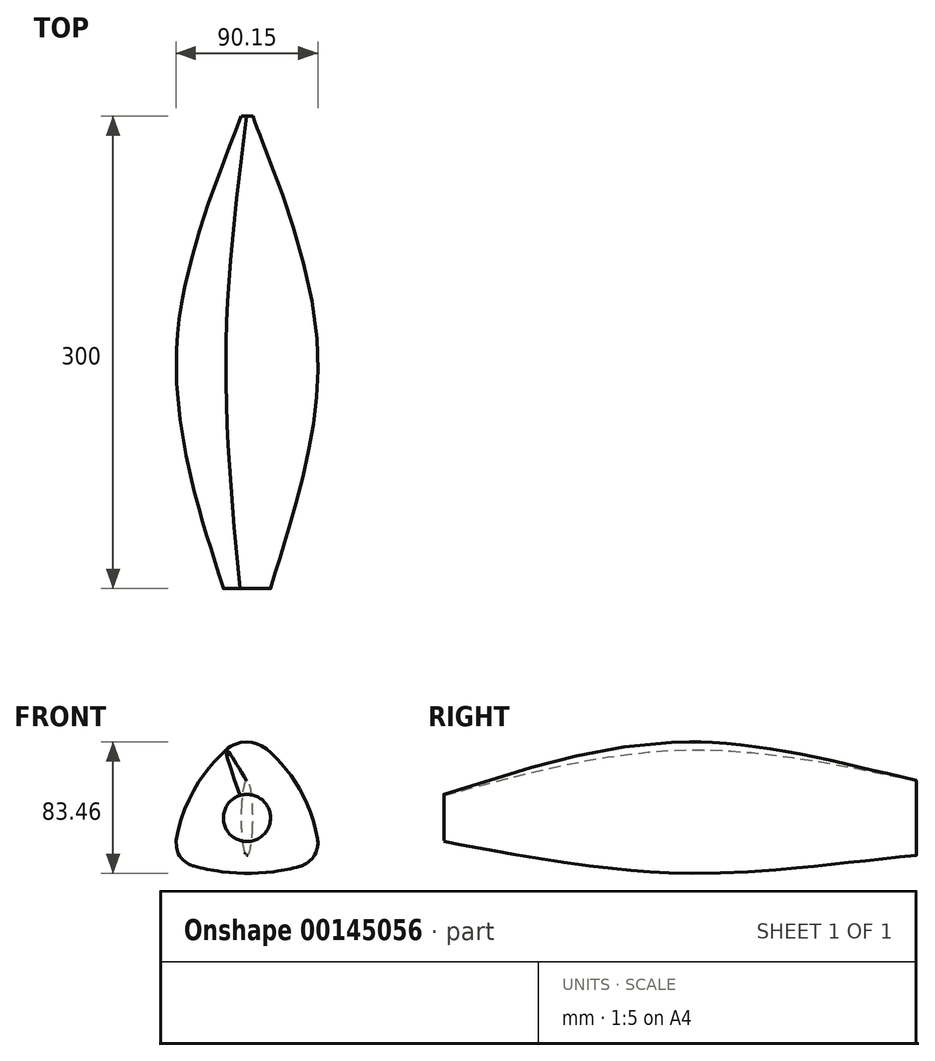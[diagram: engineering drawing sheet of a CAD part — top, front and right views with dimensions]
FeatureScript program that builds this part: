
annotation { "Feature Type Name" : "Feature", "Feature Type Description" : "" }
export const myFeature = defineFeature(function(context is Context, id is Id, definition is map)
    precondition{}
    {
        {
            var Q0;
            Q0=qCreatedBy(makeId("Front.planeOp"),FACE);
            var sketch = newSketch(context, id + "F0", { "sketchPlane" : qUnion([Q0])});
            skCircle(sketch, "E0", {"center": v(0, 0) * mm, "radius": 15 * mm});
            skSolve(sketch);
        }
        {
            var Q0;
            Q0=qCreatedBy(makeId("Front.planeOp"),FACE);
            cPlane(context, id + "F1", {"entities" : qUnion([Q0]), "cplaneType" : CPlaneType.OFFSET, "offset" : 150 * mm, "oppositeDirection" : true, "width" : 150 * mm, "height" : 150 * mm});
        }
        {
            var Q0;
            Q0=qCreatedBy(id+"F1.planeOp",FACE);
            var sketch = newSketch(context, id + "F2", { "sketchPlane" : qUnion([Q0])});
            skArc(sketch, "E1", {"start": v(-13.38, 43.09) * mm, "mid": v(-33.79, 17.42) * mm, "end": v(-44.7, -13.51) * mm});
            skArc(sketch, "E2", {"start": v(44.7, -13.51) * mm, "mid": v(33.79, 17.42) * mm, "end": v(13.38, 43.09) * mm});
            skArc(sketch, "E3", {"start": v(-33.82, -30.57) * mm, "mid": v(0, -35.05) * mm, "end": v(33.82, -30.57) * mm});
            skPoint(sketch, "E4.visualSharp", {"position": v(0, 53.21) * mm});
            skArc(sketch, "E4.filletArc", {"start": v(13.38, 43.09) * mm, "mid": v(0, 48.22) * mm, "end": v(-13.38, 43.09) * mm});
            skPoint(sketch, "E5.visualSharp", {"position": v(-46.08, -26.6) * mm});
            skArc(sketch, "E5.filletArc", {"start": v(-44.7, -13.51) * mm, "mid": v(-42.56, -24.15) * mm, "end": v(-33.82, -30.57) * mm});
            skPoint(sketch, "E6.visualSharp", {"position": v(46.08, -26.6) * mm});
            skArc(sketch, "E6.filletArc", {"start": v(33.82, -30.57) * mm, "mid": v(42.56, -24.15) * mm, "end": v(44.7, -13.51) * mm});
            skSolve(sketch);
        }
        {
            var Q0;
            Q0=qCreatedBy(makeId("Front.planeOp"),FACE);
            cPlane(context, id + "F3", {"entities" : qUnion([Q0]), "cplaneType" : CPlaneType.OFFSET, "offset" : 300 * mm, "oppositeDirection" : true, "width" : 150 * mm, "height" : 150 * mm});
        }
        {
            var Q0;
            Q0=qCreatedBy(id+"F3.planeOp",FACE);
            var sketch = newSketch(context, id + "F4", { "sketchPlane" : qUnion([Q0])});
            skEllipse(sketch, "E7", {"center": v(0, 0) * mm, "majorRadius": 3.74 * mm, "minorRadius": 23.82 * mm, "majorAxis": v(-1, 0)});
            skSolve(sketch);
        }
        {
            var Q0;
            Q0=makeQuery(id+"F0.imprint","IMPRINT",FACE,{"disambiguationData":[TD([[makeQuery(id+"F0.imprint","IMPRINT",EDGE,{"derivedFrom":sQuery(id+"F0.wireOp",EDGE,"E0")}),1.0]])]});
            var Q1;
            Q1=makeQuery(id+"F2.imprint","IMPRINT",FACE,{"disambiguationData":[TD([[makeQuery(id+"F2.imprint","IMPRINT",EDGE,{"derivedFrom":sQuery(id+"F2.wireOp",EDGE,"E1")}),1.0]])]});
            var Q2;
            Q2=makeQuery(id+"F4.imprint","IMPRINT",FACE,{"disambiguationData":[TD([[makeQuery(id+"F4.imprint","IMPRINT",EDGE,{"derivedFrom":sQuery(id+"F4.wireOp",EDGE,"E7")}),1.0]])]});
            loft(context, id + "F5", {"sheetProfilesArray" : [{ "sheetProfileEntities" : qUnion([Q0]) }, { "sheetProfileEntities" : qUnion([Q1]) }, { "sheetProfileEntities" : qUnion([Q2]) }]});
        }
    });
